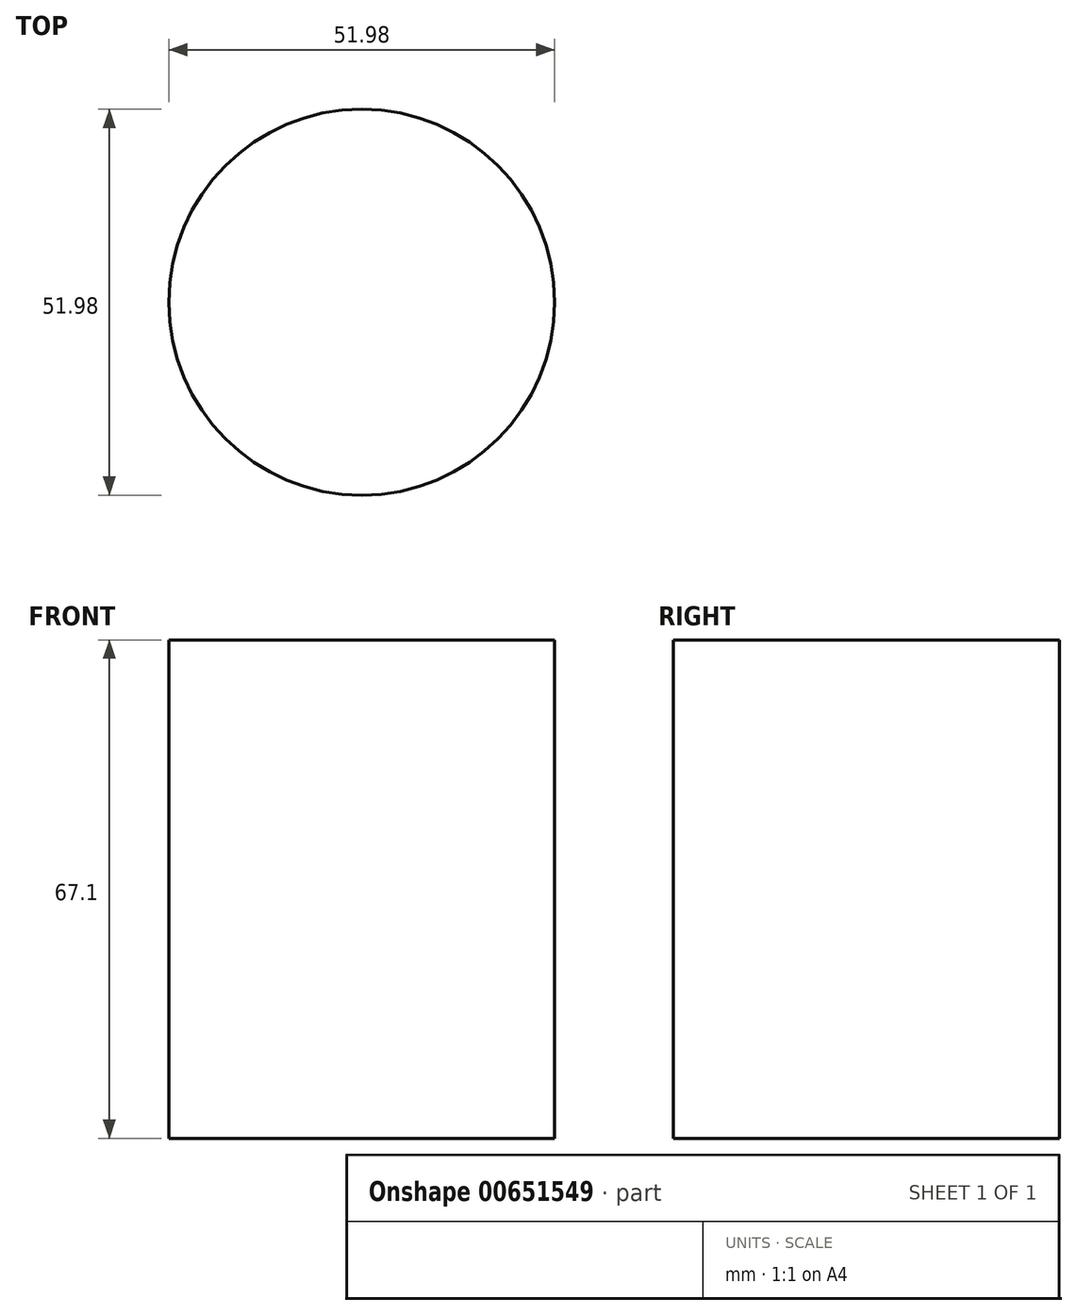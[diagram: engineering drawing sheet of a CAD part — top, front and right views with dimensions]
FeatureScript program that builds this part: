
annotation { "Feature Type Name" : "Feature", "Feature Type Description" : "" }
export const myFeature = defineFeature(function(context is Context, id is Id, definition is map)
    precondition{}
    {
        {
            var Q0;
            Q0=qCreatedBy(makeId("Top.planeOp"),FACE);
            var sketch = newSketch(context, id + "F0", { "sketchPlane" : qUnion([Q0])});
            skCircle(sketch, "E0", {"center": v(0, 0) * mm, "radius": 26 * mm});
            skSolve(sketch);
        }
        {
            var Q0;
            Q0=sQuery(id+"F0.wireOp",EDGE,"E0");
            extrude(context, id + "F1", {"bodyType" : ToolBodyType.SURFACE, "surfaceEntities" : qUnion([Q0]), "depth" : 67.1 * mm, "offsetDistance" : 25 * mm});
        }
    });
